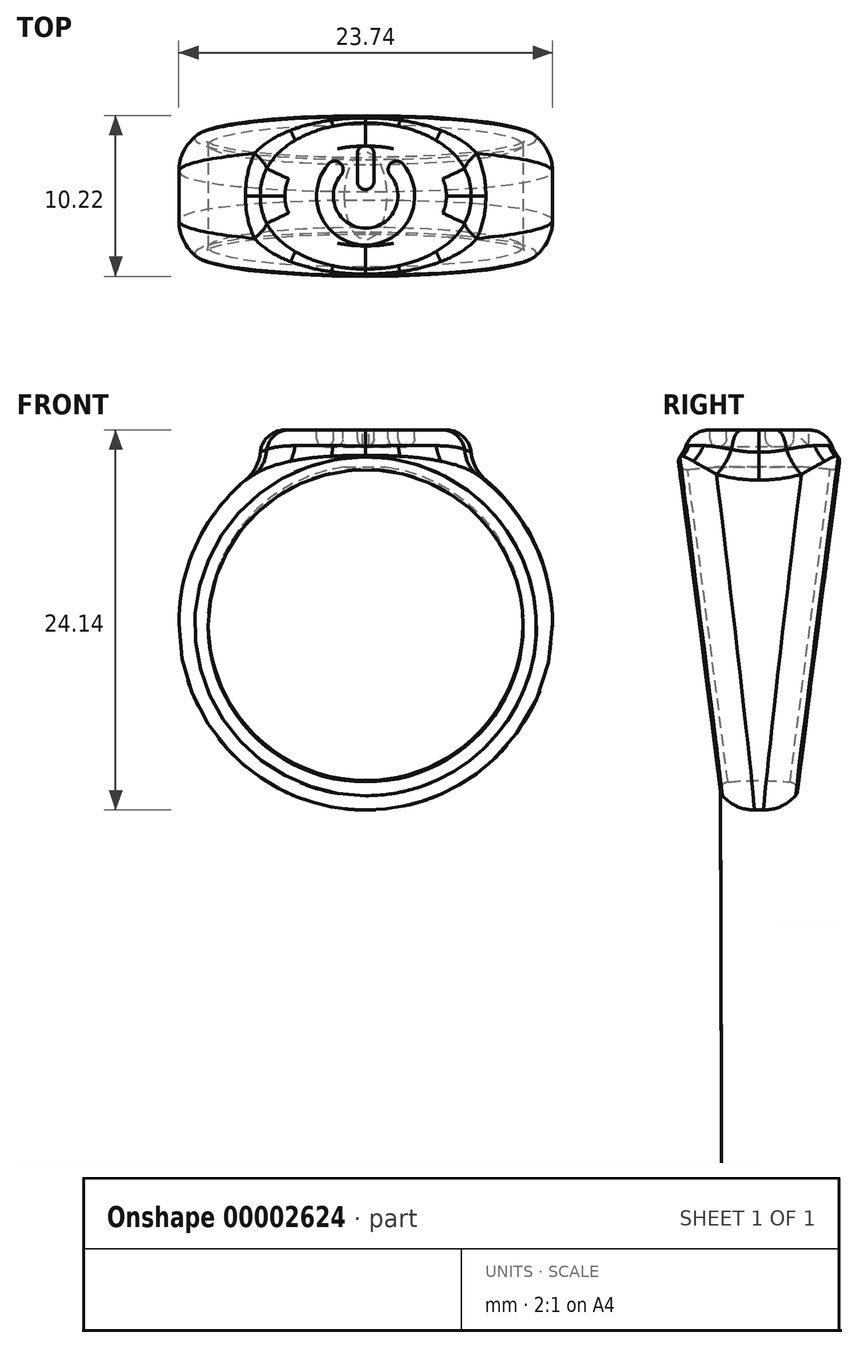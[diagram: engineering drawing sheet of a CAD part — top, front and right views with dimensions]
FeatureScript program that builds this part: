
annotation { "Feature Type Name" : "Feature", "Feature Type Description" : "" }
export const myFeature = defineFeature(function(context is Context, id is Id, definition is map)
    precondition{}
    {
        {
            var Q0;
            Q0=qCreatedBy(makeId("Front.planeOp"),FACE);
            var sketch = newSketch(context, id + "F0", { "sketchPlane" : qUnion([Q0])});
            skCircle(sketch, "E0", {"center": v(0, 0) * mm, "radius": 9.52 * mm});
            skCircle(sketch, "E1", {"center": v(0, 0) * mm, "radius": 11.3 * mm});
            skLineSegment(sketch, "E2", {"start": v(-19.06, -29.92) * mm, "end": v(20.06, -29.92) * mm, "construction": true});
            skSolve(sketch);
        }
        {
            var Q0;
            Q0=makeQuery(id+"F0.imprint","IMPRINT",FACE,{"disambiguationData":[TD([[makeQuery(id+"F0.imprint","IMPRINT",EDGE,{"derivedFrom":sQuery(id+"F0.wireOp",EDGE,"E0")}),-1.0]])]});
            var Q1;
            Q1=sQuery(id+"F0.wireOp",EDGE,"E2");
            revolve(context, id + "F1", {"entities" : qUnion([Q0]), "axis" : qUnion([Q1]), "revolveType" : RevolveType.SYMMETRIC, "angle" : 15 * degree});
        }
        {
            var Q0;
            Q0=qCreatedBy(makeId("Top.planeOp"),FACE);
            cPlane(context, id + "F2", {"entities" : qUnion([Q0]), "cplaneType" : CPlaneType.OFFSET, "offset" : 11.68 * mm, "width" : 152.4 * mm, "height" : 152.4 * mm});
        }
        {
            var Q0;
            Q0=qCreatedBy(id+"F2.planeOp",FACE);
            var sketch = newSketch(context, id + "F3", { "sketchPlane" : qUnion([Q0])});
            skLineSegment(sketch, "E3", {"start": v(-13.16, 0) * mm, "end": v(13.94, 0) * mm, "construction": true});
            skLineSegment(sketch, "E4", {"start": v(0, 6.68) * mm, "end": v(0, -7.16) * mm, "construction": true});
            skFitSpline(sketch, "E5", {"points": [v(-6.35, 0) * mm, v(0, 4.24) * mm], "startDerivative": vector(-0.42, 8.09) * mm, "endDerivative": vector(8.17, -0.21) * mm});
            skFitSpline(sketch, "E6.0.MirrorCS", {"points": [v(6.35, 0) * mm, v(0, 4.24) * mm], "startDerivative": vector(0.42, 8.09) * mm, "endDerivative": vector(-8.17, -0.21) * mm});
            skFitSpline(sketch, "E7.0.MirrorCS", {"points": [v(-6.35, 0) * mm, v(0, -4.24) * mm], "startDerivative": vector(-0.42, -8.09) * mm, "endDerivative": vector(8.17, 0.21) * mm});
            skFitSpline(sketch, "E8.0.MirrorCS", {"points": [v(6.35, 0) * mm, v(0, -4.24) * mm], "startDerivative": vector(0.42, -8.09) * mm, "endDerivative": vector(-8.17, 0.21) * mm});
            skSolve(sketch);
        }
        {
            var Q0;
            Q0=makeQuery(id+"F3.imprint","IMPRINT",FACE,{"disambiguationData":[TD([[makeQuery(id+"F3.imprint","IMPRINT",EDGE,{"derivedFrom":sQuery(id+"F3.wireOp",EDGE,"E5")}),-1.0]])]});
            extrude(context, id + "F4", {"entities" : qUnion([Q0]), "operationType" : NewBodyOperationType.ADD, "oppositeDirection" : true, "depth" : 2.25 * mm});
        }
        {
            var Q0;
            Q0=makeQuery(id+"F1.opRevolve","CAP_EDGE",EDGE,{"disambiguationData":[OSD([sQuery(id+"F0.wireOp",EDGE,"E1")])],"isStart":false});
            var Q1;
            Q1=makeQuery(id+"F1.opRevolve","CAP_EDGE",EDGE,{"disambiguationData":[OSD([sQuery(id+"F0.wireOp",EDGE,"E1")])],"isStart":true});
            fillet(context, id + "F5", {"entities" : qUnion([Q0, Q1]), "radius" : 2.54 * mm, "tangentPropagation" : true, "allowEdgeOverflow" : false});
        }
        {
            var Q0;
            Q0=makeQuery(id+"F5.opFillet","BLEND_EDGE",EDGE,{"blendedFrom":[makeQuery(id+"F1.opRevolve","CAP_EDGE",EDGE,{"disambiguationData":[OSD([sQuery(id+"F0.wireOp",EDGE,"E1")])],"isStart":false}),makeQuery(id+"F4.opExtrude","SWEPT_FACE",FACE,{"disambiguationData":[OSD([sQuery(id+"F3.wireOp",EDGE,"E7.0.MirrorCS")])]})],"blendedInto":[makeQuery(id+"F4.opExtrude","SWEPT_FACE",FACE,{"disambiguationData":[OSD([sQuery(id+"F3.wireOp",EDGE,"E7.0.MirrorCS")])]})]});
            var Q1;
            Q1=makeQuery(id+"F5.opFillet","BLEND_EDGE",EDGE,{"blendedFrom":[makeQuery(id+"F1.opRevolve","CAP_EDGE",EDGE,{"disambiguationData":[OSD([sQuery(id+"F0.wireOp",EDGE,"E1")])],"isStart":false}),makeQuery(id+"F4.opExtrude","SWEPT_FACE",FACE,{"disambiguationData":[OSD([sQuery(id+"F3.wireOp",EDGE,"E8.0.MirrorCS")])]})],"blendedInto":[makeQuery(id+"F4.opExtrude","SWEPT_FACE",FACE,{"disambiguationData":[OSD([sQuery(id+"F3.wireOp",EDGE,"E8.0.MirrorCS")])]})]});
            var Q2;
            Q2=makeQuery(id+"F4.boolean.opBoolean","INTERSECT",EDGE,{"derivedFrom":[makeQuery(id+"F1.opRevolve","SWEPT_FACE",FACE,{"disambiguationData":[OSD([sQuery(id+"F0.wireOp",EDGE,"E1")])]}),makeQuery(id+"F4.opExtrude","SWEPT_FACE",FACE,{"disambiguationData":[OSD([sQuery(id+"F3.wireOp",EDGE,"E8.0.MirrorCS")])]})]});
            var Q3;
            Q3=makeQuery(id+"F4.opExtrude","CAP_EDGE",EDGE,{"disambiguationData":[OSD([sQuery(id+"F3.wireOp",EDGE,"E7.0.MirrorCS")])],"isStart":false});
            var Q4;
            Q4=makeQuery(id+"F4.opExtrude","CAP_EDGE",EDGE,{"disambiguationData":[OSD([sQuery(id+"F3.wireOp",EDGE,"E5")])],"isStart":false});
            var Q5;
            Q5=makeQuery(id+"F4.boolean.opBoolean","INTERSECT",EDGE,{"derivedFrom":[makeQuery(id+"F1.opRevolve","SWEPT_FACE",FACE,{"disambiguationData":[OSD([sQuery(id+"F0.wireOp",EDGE,"E1")])]}),makeQuery(id+"F4.opExtrude","SWEPT_FACE",FACE,{"disambiguationData":[OSD([sQuery(id+"F3.wireOp",EDGE,"E5")])]})]});
            var Q6;
            Q6=makeQuery(id+"F5.opFillet","BLEND_EDGE",EDGE,{"blendedFrom":[makeQuery(id+"F1.opRevolve","CAP_EDGE",EDGE,{"disambiguationData":[OSD([sQuery(id+"F0.wireOp",EDGE,"E1")])],"isStart":true}),makeQuery(id+"F4.opExtrude","SWEPT_FACE",FACE,{"disambiguationData":[OSD([sQuery(id+"F3.wireOp",EDGE,"E5")])]})],"blendedInto":[makeQuery(id+"F4.opExtrude","SWEPT_FACE",FACE,{"disambiguationData":[OSD([sQuery(id+"F3.wireOp",EDGE,"E5")])]})]});
            var Q7;
            Q7=makeQuery(id+"F5.opFillet","BLEND_EDGE",EDGE,{"blendedFrom":[makeQuery(id+"F1.opRevolve","CAP_EDGE",EDGE,{"disambiguationData":[OSD([sQuery(id+"F0.wireOp",EDGE,"E1")])],"isStart":true}),makeQuery(id+"F4.opExtrude","SWEPT_FACE",FACE,{"disambiguationData":[OSD([sQuery(id+"F3.wireOp",EDGE,"E6.0.MirrorCS")])]})],"blendedInto":[makeQuery(id+"F4.opExtrude","SWEPT_FACE",FACE,{"disambiguationData":[OSD([sQuery(id+"F3.wireOp",EDGE,"E6.0.MirrorCS")])]})]});
            fillet(context, id + "F6", {"entities" : qUnion([Q0, Q1, Q2, Q3, Q4, Q5, Q6, Q7]), "radius" : 2.54 * mm, "tangentPropagation" : true, "allowEdgeOverflow" : false});
        }
        {
            var Q0;
            {var subQ0=makeQuery(id+"F4.opExtrude","CAP_EDGE",EDGE,{"disambiguationData":[OSD([sQuery(id+"F3.wireOp",EDGE,"E7.0.MirrorCS")])],"isStart":true});Q0=qUnion([subQ0,subQ0]);}
            var Q1;
            {var subQ0=makeQuery(id+"F4.opExtrude","CAP_EDGE",EDGE,{"disambiguationData":[OSD([sQuery(id+"F3.wireOp",EDGE,"E5")])],"isStart":true});Q1=qUnion([subQ0,subQ0]);}
            var Q2;
            {var subQ0=makeQuery(id+"F4.opExtrude","CAP_EDGE",EDGE,{"disambiguationData":[OSD([sQuery(id+"F3.wireOp",EDGE,"E8.0.MirrorCS")])],"isStart":true});Q2=qUnion([subQ0,subQ0]);}
            var Q3;
            {var subQ0=makeQuery(id+"F4.opExtrude","CAP_EDGE",EDGE,{"disambiguationData":[OSD([sQuery(id+"F3.wireOp",EDGE,"E6.0.MirrorCS")])],"isStart":true});Q3=qUnion([subQ0,subQ0]);}
            fillet(context, id + "F7", {"entities" : qUnion([Q0, Q1, Q2, Q3]), "radius" : 1.5 * mm, "tangentPropagation" : true, "allowEdgeOverflow" : false});
        }
        {
            var Q0;
            Q0=makeQuery(id+"F4.opExtrude","CAP_FACE",FACE,{"disambiguationData":[OSD([sQuery(id+"F3.wireOp",EDGE,"E5"),sQuery(id+"F3.wireOp",EDGE,"E6.0.MirrorCS"),sQuery(id+"F3.wireOp",EDGE,"E7.0.MirrorCS"),sQuery(id+"F3.wireOp",EDGE,"E8.0.MirrorCS")])],"isStart":true});
            var sketch = newSketch(context, id + "F8", { "sketchPlane" : qUnion([Q0])});
            skArc(sketch, "E9", {"start": v(-1.48, 1.27) * mm, "mid": v(0, -1.95) * mm, "end": v(1.48, 1.27) * mm});
            skArc(sketch, "E10", {"start": v(-2.25, 1.93) * mm, "mid": v(0, -2.97) * mm, "end": v(2.25, 1.93) * mm});
            skLineSegment(sketch, "E11", {"start": v(-1.47, 1.91) * mm, "end": v(-1.47, 1.91) * mm});
            skLineSegment(sketch, "E12", {"start": v(1.47, 1.91) * mm, "end": v(1.47, 1.91) * mm});
            skLineSegment(sketch, "E13", {"start": v(0, -3.6) * mm, "end": v(0, 3.87) * mm, "construction": true});
            skPoint(sketch, "E14.orphan", {"position": v(-2.72, 3.55) * mm});
            skPoint(sketch, "E15.orphan", {"position": v(2.72, 3.55) * mm});
            skPoint(sketch, "E16.visualSharp", {"position": v(-1.8, 2.36) * mm});
            skArc(sketch, "E16.filletArc", {"start": v(-1.47, 1.91) * mm, "mid": v(-1.86, 2.1) * mm, "end": v(-2.25, 1.93) * mm});
            skPoint(sketch, "E17.visualSharp", {"position": v(-1.19, 1.55) * mm});
            skArc(sketch, "E17.filletArc", {"start": v(-1.48, 1.27) * mm, "mid": v(-1.36, 1.59) * mm, "end": v(-1.47, 1.91) * mm});
            skPoint(sketch, "E18.visualSharp", {"position": v(1.19, 1.55) * mm});
            skArc(sketch, "E18.filletArc", {"start": v(1.47, 1.91) * mm, "mid": v(1.36, 1.59) * mm, "end": v(1.48, 1.27) * mm});
            skPoint(sketch, "E19.visualSharp", {"position": v(1.8, 2.36) * mm});
            skArc(sketch, "E19.filletArc", {"start": v(2.25, 1.93) * mm, "mid": v(1.86, 2.1) * mm, "end": v(1.47, 1.91) * mm});
            skLineSegment(sketch, "E20", {"start": v(-0.5, 2.55) * mm, "end": v(-0.5, 0.9) * mm});
            skArc(sketch, "E21", {"start": v(-0.5, 0.9) * mm, "mid": v(0, 0.4) * mm, "end": v(0.5, 0.9) * mm});
            skArc(sketch, "E22", {"start": v(0.5, 2.55) * mm, "mid": v(0, 3.06) * mm, "end": v(-0.5, 2.55) * mm});
            skLineSegment(sketch, "E23.0.MirrorCS", {"start": v(0.5, 2.55) * mm, "end": v(0.5, 0.9) * mm});
            skSolve(sketch);
        }
        {
            var Q0;
            Q0=makeQuery(id+"F8.imprint","IMPRINT",FACE,{"disambiguationData":[TD([[makeQuery(id+"F8.imprint","IMPRINT",EDGE,{"derivedFrom":sQuery(id+"F8.wireOp",EDGE,"E9")}),-1.0]])]});
            var Q1;
            {var subQ10=sQuery(id+"F8.wireOp",EDGE,"E20");Q1=makeQuery(id+"F8.imprint","IMPRINT",FACE,{"disambiguationData":[TD([[makeQuery(id+"F8.imprint","IMPRINT",EDGE,{"derivedFrom":subQ10}),1.0]])]});}
            extrude(context, id + "F9", {"entities" : qUnion([Q0, Q1]), "operationType" : NewBodyOperationType.REMOVE, "oppositeDirection" : true, "depth" : 1.02 * mm});
        }
        {
            var Q0;
            Q0=makeQuery(id+"F9.opExtrude","CAP_EDGE",EDGE,{"disambiguationData":[OSD([sQuery(id+"F8.wireOp",EDGE,"E10")])],"isStart":false});
            var Q1;
            Q1=makeQuery(id+"F9.opExtrude","CAP_EDGE",EDGE,{"disambiguationData":[OSD([sQuery(id+"F8.wireOp",EDGE,"E9")])],"isStart":false});
            var Q2;
            Q2=makeQuery(id+"F9.opExtrude","CAP_EDGE",EDGE,{"disambiguationData":[OSD([sQuery(id+"F8.wireOp",EDGE,"E16.filletArc"),sQuery(id+"F8.wireOp",EDGE,"E17.filletArc")])],"isStart":false});
            var Q3;
            Q3=makeQuery(id+"F9.opExtrude","CAP_EDGE",EDGE,{"disambiguationData":[OSD([sQuery(id+"F8.wireOp",EDGE,"E18.filletArc"),sQuery(id+"F8.wireOp",EDGE,"E19.filletArc")])],"isStart":false});
            var Q4;
            Q4=makeQuery(id+"F9.opExtrude","CAP_EDGE",EDGE,{"disambiguationData":[OSD([sQuery(id+"F8.wireOp",EDGE,"E21")])],"isStart":false});
            var Q5;
            Q5=makeQuery(id+"F9.opExtrude","CAP_EDGE",EDGE,{"disambiguationData":[OSD([sQuery(id+"F8.wireOp",EDGE,"E23.0.MirrorCS")])],"isStart":false});
            var Q6;
            Q6=makeQuery(id+"F9.opExtrude","CAP_EDGE",EDGE,{"disambiguationData":[OSD([sQuery(id+"F8.wireOp",EDGE,"E20")])],"isStart":false});
            var Q7;
            Q7=makeQuery(id+"F9.opExtrude","CAP_EDGE",EDGE,{"disambiguationData":[OSD([sQuery(id+"F8.wireOp",EDGE,"E22")])],"isStart":false});
            var Q8;
            Q8=makeQuery(id+"F9.boolean.opBoolean","COPY",EDGE,{"derivedFrom":makeQuery(id+"F9.opExtrude","CAP_EDGE",EDGE,{"disambiguationData":[OSD([sQuery(id+"F8.wireOp",EDGE,"E10")])],"isStart":false})});
            var Q9;
            Q9=makeQuery(id+"F9.boolean.opBoolean","COPY",EDGE,{"derivedFrom":makeQuery(id+"F9.opExtrude","CAP_EDGE",EDGE,{"disambiguationData":[OSD([sQuery(id+"F8.wireOp",EDGE,"E20")])],"isStart":false})});
            fillet(context, id + "F10", {"entities" : qUnion([Q0, Q1, Q2, Q3, Q4, Q5, Q6, Q7, Q8, Q9]), "radius" : 0.5 * mm, "tangentPropagation" : true, "allowEdgeOverflow" : false});
        }
        {
            var Q0;
            Q0=makeQuery(id+"F5.opFillet","BLEND_EDGE",EDGE,{"blendedFrom":[makeQuery(id+"F1.opRevolve","CAP_EDGE",EDGE,{"disambiguationData":[OSD([sQuery(id+"F0.wireOp",EDGE,"E1")])],"isStart":false}),makeQuery(id+"F1.opRevolve","SWEPT_FACE",FACE,{"disambiguationData":[OSD([sQuery(id+"F0.wireOp",EDGE,"E0")])]})],"blendedInto":[makeQuery(id+"F1.opRevolve","SWEPT_FACE",FACE,{"disambiguationData":[OSD([sQuery(id+"F0.wireOp",EDGE,"E0")])]})]});
            var Q1;
            Q1=makeQuery(id+"F5.opFillet","BLEND_EDGE",EDGE,{"blendedFrom":[makeQuery(id+"F1.opRevolve","CAP_EDGE",EDGE,{"disambiguationData":[OSD([sQuery(id+"F0.wireOp",EDGE,"E1")])],"isStart":true}),makeQuery(id+"F1.opRevolve","SWEPT_FACE",FACE,{"disambiguationData":[OSD([sQuery(id+"F0.wireOp",EDGE,"E0")])]})],"blendedInto":[makeQuery(id+"F1.opRevolve","SWEPT_FACE",FACE,{"disambiguationData":[OSD([sQuery(id+"F0.wireOp",EDGE,"E0")])]})]});
            fillet(context, id + "F11", {"entities" : qUnion([Q0, Q1]), "radius" : .5 * mm, "tangentPropagation" : true, "allowEdgeOverflow" : false});
        }
        {
            var Q0;
            Q0=makeQuery(id+"F1.opRevolve","SWEPT_BODY",BODY,{"disambiguationData":[OSD([sQuery(id+"F0.wireOp",EDGE,"E0"),sQuery(id+"F0.wireOp",EDGE,"E1")])]});
            var Q1;
            Q1=qCreatedBy(makeId("Origin.pointOp"),VERTEX);
            transform(context, id + "F12", {"entities" : qUnion([Q0]), "transformType" : TransformType.SCALE_UNIFORMLY, "scale" : 1.05, "makeCopy" : false, "scalePoint" : qUnion([Q1])});
        }
    });
